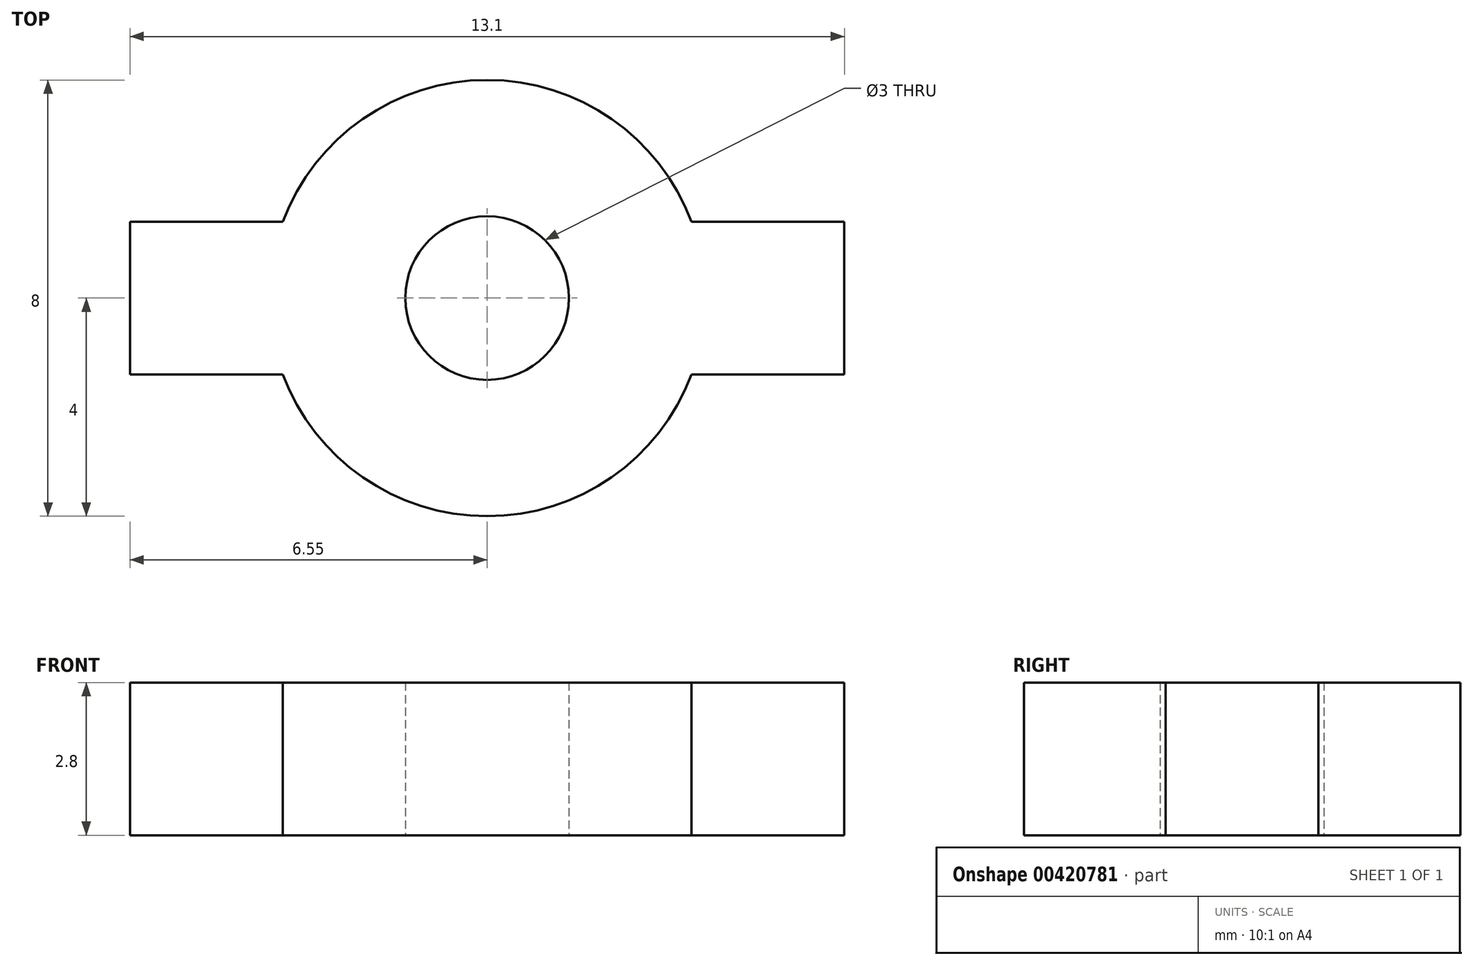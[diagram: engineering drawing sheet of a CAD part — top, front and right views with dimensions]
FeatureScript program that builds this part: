
annotation { "Feature Type Name" : "Feature", "Feature Type Description" : "" }
export const myFeature = defineFeature(function(context is Context, id is Id, definition is map)
    precondition{}
    {
        {
            var Q0;
            Q0=qCreatedBy(makeId("Top.planeOp"),FACE);
            var sketch = newSketch(context, id + "F0", { "sketchPlane" : qUnion([Q0])});
            skCircle(sketch, "E0", {"center": v(0, 0) * mm, "radius": 4 * mm});
            skLineSegment(sketch, "E1.bottom", {"start": v(-3.75, 1.4) * mm, "end": v(-6.55, 1.4) * mm});
            skLineSegment(sketch, "E1.top", {"start": v(-3.75, -1.4) * mm, "end": v(-6.55, -1.4) * mm});
            skLineSegment(sketch, "E1.left", {"start": v(-3.75, 1.4) * mm, "end": v(-3.75, -1.4) * mm});
            skLineSegment(sketch, "E1.right", {"start": v(-6.55, 1.4) * mm, "end": v(-6.55, -1.4) * mm});
            skPoint(sketch, "E1.middle", {"position": v(-5.15, 0) * mm});
            skLineSegment(sketch, "E2.bottom", {"start": v(3.75, 1.4) * mm, "end": v(6.55, 1.4) * mm});
            skLineSegment(sketch, "E2.top", {"start": v(3.75, -1.4) * mm, "end": v(6.55, -1.4) * mm});
            skLineSegment(sketch, "E2.left", {"start": v(3.75, 1.4) * mm, "end": v(3.75, -1.4) * mm});
            skLineSegment(sketch, "E2.right", {"start": v(6.55, 1.4) * mm, "end": v(6.55, -1.4) * mm});
            skPoint(sketch, "E2.middle", {"position": v(5.15, 0) * mm});
            skCircle(sketch, "E3", {"center": v(0, 0) * mm, "radius": 1.5 * mm});
            skSolve(sketch);
        }
        {
            var Q0;
            {var subQ1=sQuery(id+"F0.wireOp",EDGE,"E1.bottom");Q0=makeQuery(id+"F0.imprint","IMPRINT",FACE,{"disambiguationData":[TD([[makeQuery(id+"F0.imprint","IMPRINT",EDGE,{"derivedFrom":subQ1}),1.0]])]});}
            var Q1;
            {var subQ0=sQuery(id+"F0.wireOp",EDGE,"E1.left");Q1=makeQuery(id+"F0.imprint","IMPRINT",FACE,{"disambiguationData":[TD([[makeQuery(id+"F0.imprint","IMPRINT",EDGE,{"derivedFrom":subQ0}),1.0]])]});}
            var Q2;
            {var subQ0=sQuery(id+"F0.wireOp",EDGE,"E1.left");Q2=makeQuery(id+"F0.imprint","IMPRINT",FACE,{"disambiguationData":[TD([[makeQuery(id+"F0.imprint","IMPRINT",EDGE,{"derivedFrom":subQ0}),-1.0]])]});}
            var Q3;
            {var subQ1=sQuery(id+"F0.wireOp",EDGE,"E2.bottom");Q3=makeQuery(id+"F0.imprint","IMPRINT",FACE,{"disambiguationData":[TD([[makeQuery(id+"F0.imprint","IMPRINT",EDGE,{"derivedFrom":subQ1}),-1.0]])]});}
            var Q4;
            {var subQ0=sQuery(id+"F0.wireOp",EDGE,"E2.left");Q4=makeQuery(id+"F0.imprint","IMPRINT",FACE,{"disambiguationData":[TD([[makeQuery(id+"F0.imprint","IMPRINT",EDGE,{"derivedFrom":subQ0}),1.0]])]});}
            extrude(context, id + "F1", {"entities" : qUnion([Q0, Q1, Q2, Q3, Q4]), "depth" : 2.8 * mm});
        }
    });
